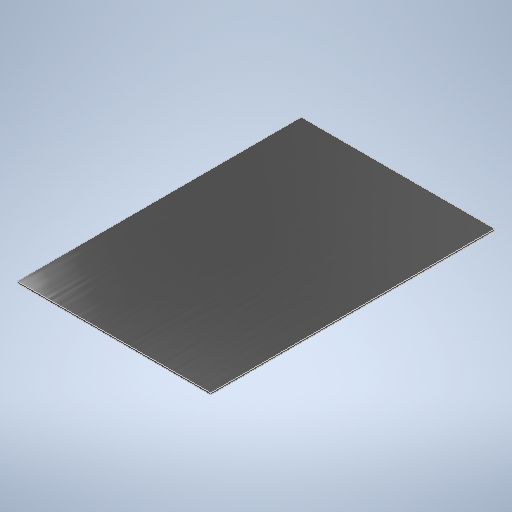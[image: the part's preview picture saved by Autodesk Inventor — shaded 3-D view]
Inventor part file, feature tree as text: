
AUTODESK INVENTOR PART (.ipt)
format: ipt  version: 2025.1 (Build 291241020, 241B)  size: 241,152 bytes
history: native  units: in
note: dims shown in document units (in); Inventor stores cm internally (conversion verified against a paired STEP export)
features: extrude x1, sketch x1
ambient origin geometry x8: Origin, YZ Plane, XZ Plane, XY Plane, X Axis, Y Axis, Z Axis, Center Point
bodies: Solid1 (feature_tree)
feature tree (2):
  extrude  "Extrusion1"  Depth=19.45in
  sketch  "Sketch1"  dims[d0=13.25in d1=19.45in d2=0.125in d3=0.0in]
